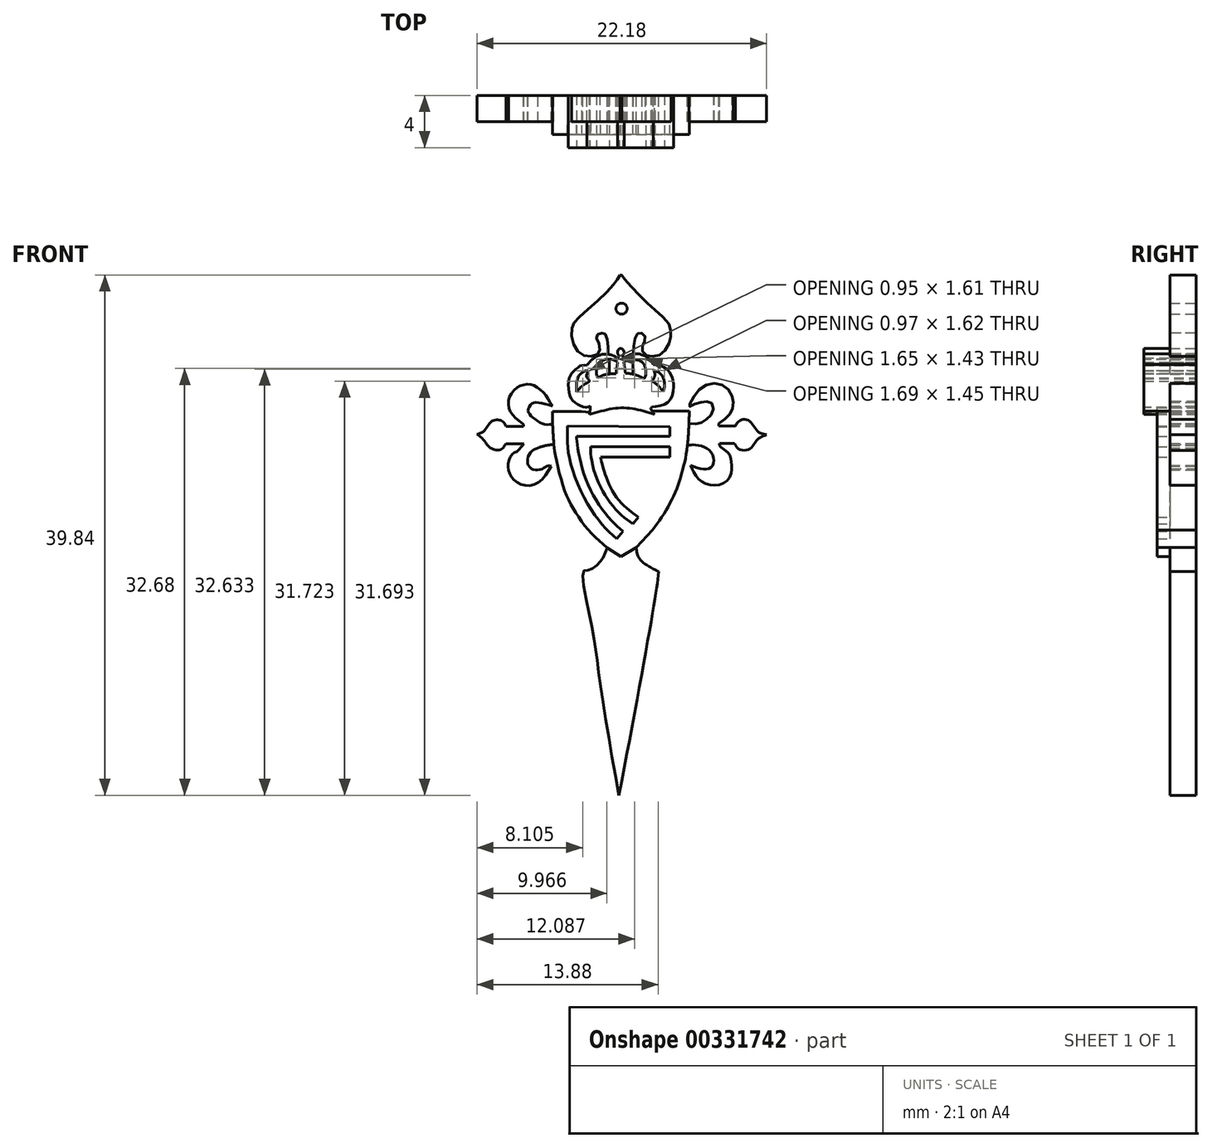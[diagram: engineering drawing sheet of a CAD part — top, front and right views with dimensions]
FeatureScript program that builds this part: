
annotation { "Feature Type Name" : "Feature", "Feature Type Description" : "" }
export const myFeature = defineFeature(function(context is Context, id is Id, definition is map)
    precondition{}
    {
        {
            var Q0;
            Q0=qCreatedBy(makeId("Front.planeOp"),FACE);
            var sketch = newSketch(context, id + "F0", { "sketchPlane" : qUnion([Q0])});
            skPoint(sketch, "E0.7.internal.snap0", {"position": v(-12.21, 0) * mm});
            skFitSpline(sketch, "E0", {"points": [v(-13.1, 18.95) * mm, v(-13.44, 18.18) * mm, v(-13.89, 17.63) * mm, v(-14.59, 17.23) * mm, v(-14.94, 17.13) * mm, v(-14.34, 13.19) * mm, v(-13.74, 9.24) * mm, v(-12.21, 0) * mm], "startDerivative": vector(-3.46, -9.08) * mm, "endDerivative": vector(6.22, -33.66) * mm});
            skFitSpline(sketch, "E1", {"points": [v(-12.21, 0) * mm, v(-9.51, 14.73) * mm, v(-9.16, 17.13) * mm], "startDerivative": vector(4.73, 24.16) * mm, "endDerivative": vector(0.84, 6.55) * mm});
            skFitSpline(sketch, "E2", {"points": [v(-9.16, 17.13) * mm, v(-9.97, 17.55) * mm, v(-10.68, 18.18) * mm, v(-10.9, 18.97) * mm], "startDerivative": vector(-2.4, 1.14) * mm, "endDerivative": vector(-0.33, 2.58) * mm});
            skFitSpline(sketch, "E3", {"points": [v(-10.9, 18.97) * mm, v(-12.07, 18.28) * mm], "startDerivative": vector(-1.18, -0.68) * mm, "endDerivative": vector(-1.18, -0.68) * mm});
            skFitSpline(sketch, "E4", {"points": [v(-13.1, 18.95) * mm, v(-12.07, 18.28) * mm], "startDerivative": vector(1.04, -0.67) * mm, "endDerivative": vector(1.04, -0.67) * mm});
            skFitSpline(sketch, "E5", {"points": [v(-13.1, 18.95) * mm, v(-14.59, 20.35) * mm, v(-15.72, 21.96) * mm, v(-16.47, 23.62) * mm, v(-17.1, 26.19) * mm, v(-17.2, 27.07) * mm, v(-17.3, 28.41) * mm, v(-17.31, 29.4) * mm], "startDerivative": vector(-9.68, 8.24) * mm, "endDerivative": vector(-0.07, 8.24) * mm});
            skFitSpline(sketch, "E6", {"points": [v(-10.9, 18.97) * mm, v(-9.64, 20.3) * mm], "startDerivative": vector(1.25, 1.34) * mm, "endDerivative": vector(1.25, 1.34) * mm});
            skFitSpline(sketch, "E7", {"points": [v(-9.64, 20.3) * mm, v(-8.68, 21.71) * mm, v(-7.88, 23.27) * mm, v(-7.35, 24.84) * mm, v(-7, 26.54) * mm, v(-6.85, 28.48) * mm, v(-6.83, 29.42) * mm], "startDerivative": vector(5.8, 8.01) * mm, "endDerivative": vector(0.09, 6.64) * mm});
            skFitSpline(sketch, "E8", {"points": [v(-17.31, 29.4) * mm, v(-15.09, 29.4) * mm], "startDerivative": vector(2.23, 0) * mm, "endDerivative": vector(2.23, 0) * mm});
            skFitSpline(sketch, "E9", {"points": [v(-6.83, 29.42) * mm, v(-9.14, 29.42) * mm], "startDerivative": vector(-2.31, 0) * mm, "endDerivative": vector(-2.31, 0) * mm});
            skFitSpline(sketch, "E10", {"points": [v(-17.3, 28.41) * mm, v(-17.94, 28.41) * mm, v(-18.45, 28.66) * mm, v(-18.98, 29.1) * mm, v(-19.15, 29.4) * mm, v(-19.1, 29.73) * mm, v(-18.84, 30) * mm, v(-18.36, 30.07) * mm, v(-17.3, 29.81) * mm], "startDerivative": vector(-5, -0.45) * mm, "endDerivative": vector(6.48, -1.86) * mm});
            skFitSpline(sketch, "E11", {"points": [v(-17.3, 29.81) * mm, v(-17.7, 30.43) * mm, v(-18.06, 30.9) * mm, v(-18.59, 31.3) * mm, v(-18.98, 31.47) * mm, v(-19.6, 31.41) * mm, v(-20.02, 31.22) * mm, v(-20.5, 30.68) * mm, v(-20.67, 30.15) * mm, v(-20.61, 29.59) * mm, v(-20.28, 29.05) * mm, v(-19.52, 28.4) * mm], "startDerivative": vector(-3.97, 6.53) * mm, "endDerivative": vector(7.28, -5.63) * mm});
            skFitSpline(sketch, "E12", {"points": [v(-19.52, 28.4) * mm, v(-19.52, 28.18) * mm], "startDerivative": vector(0, -0.22) * mm, "endDerivative": vector(0, -0.22) * mm});
            skFitSpline(sketch, "E13", {"points": [v(-19.52, 28.26) * mm, v(-20.87, 28.26) * mm], "startDerivative": vector(-1.35, 0) * mm, "endDerivative": vector(-1.35, 0) * mm});
            skFitSpline(sketch, "E14", {"points": [v(-20.87, 28.26) * mm, v(-21.15, 28.66) * mm, v(-21.51, 28.74) * mm, v(-21.93, 28.66) * mm, v(-22.27, 28.26) * mm, v(-22.6, 27.84) * mm, v(-23.09, 27.65) * mm], "startDerivative": vector(-1.46, 2.85) * mm, "endDerivative": vector(-2.96, -0.84) * mm});
            skFitSpline(sketch, "E15", {"points": [v(-23.09, 27.65) * mm, v(-22.64, 27.28) * mm, v(-22.16, 26.7) * mm, v(-21.7, 26.47) * mm, v(-21.23, 26.5) * mm, v(-20.87, 26.92) * mm], "startDerivative": vector(2.3, -1.54) * mm, "endDerivative": vector(1.63, 2.61) * mm});
            skFitSpline(sketch, "E16", {"points": [v(-20.87, 26.92) * mm, v(-19.49, 26.92) * mm], "startDerivative": vector(1.38, 0) * mm, "endDerivative": vector(1.38, 0) * mm});
            skFitSpline(sketch, "E17", {"points": [v(-19.49, 26.92) * mm, v(-20, 26.36) * mm, v(-20.33, 26.16) * mm, v(-20.67, 25.54) * mm, v(-20.67, 24.95) * mm, v(-20.36, 24.25) * mm, v(-19.49, 23.74) * mm, v(-18.36, 23.97) * mm, v(-17.4, 25.2) * mm], "startDerivative": vector(-4.32, -5.68) * mm, "endDerivative": vector(4.95, 8.5) * mm});
            skFitSpline(sketch, "E18", {"points": [v(-17.4, 25.2) * mm, v(-17.7, 25.2) * mm, v(-18.14, 24.98) * mm, v(-18.84, 24.98) * mm, v(-19.2, 25.46) * mm, v(-19.01, 26.21) * mm, v(-18.42, 26.6) * mm], "startDerivative": vector(-2.4, 0.38) * mm, "endDerivative": vector(3.59, 1.63) * mm});
            skFitSpline(sketch, "E19", {"points": [v(-17.2, 26.87) * mm, v(-17.7, 26.8) * mm, v(-18.42, 26.6) * mm], "startDerivative": vector(-1.06, -0.09) * mm, "endDerivative": vector(-1.39, -0.42) * mm});
            skFitSpline(sketch, "E20", {"points": [v(-6.85, 28.48) * mm, v(-6.05, 28.48) * mm, v(-5.5, 28.8) * mm, v(-5.01, 29.42) * mm, v(-5.16, 30.07) * mm, v(-5.72, 30.12) * mm, v(-6.45, 29.95) * mm, v(-6.83, 29.76) * mm, v(-6.48, 30.54) * mm, v(-5.46, 31.44) * mm, v(-4.23, 31.39) * mm, v(-3.55, 30.57) * mm, v(-3.47, 29.78) * mm, v(-3.75, 29.14) * mm, v(-4.57, 28.48) * mm], "startDerivative": vector(11.98, -1.22) * mm, "endDerivative": vector(-11.46, -7.82) * mm});
            skFitSpline(sketch, "E21", {"points": [v(-4.57, 28.48) * mm, v(-4.57, 28.18) * mm], "startDerivative": vector(0, -0.3) * mm, "endDerivative": vector(0, -0.3) * mm});
            skFitSpline(sketch, "E22", {"points": [v(-4.57, 28.28) * mm, v(-3.3, 28.28) * mm], "startDerivative": vector(1.26, 0) * mm, "endDerivative": vector(1.26, 0) * mm});
            skFitSpline(sketch, "E23", {"points": [v(-3.3, 28.28) * mm, v(-2.96, 28.69) * mm, v(-2.26, 28.69) * mm, v(-1.59, 27.87) * mm, v(-0.91, 27.62) * mm], "startDerivative": vector(1.23, 2.21) * mm, "endDerivative": vector(2.92, -0.45) * mm});
            skFitSpline(sketch, "E24", {"points": [v(-3.36, 26.95) * mm, v(-3.05, 26.52) * mm, v(-2.23, 26.5) * mm, v(-1.78, 27.03) * mm, v(-1.47, 27.34) * mm, v(-0.91, 27.62) * mm], "startDerivative": vector(1.14, -2.62) * mm, "endDerivative": vector(3.03, 1.34) * mm});
            skFitSpline(sketch, "E25", {"points": [v(-3.36, 26.95) * mm, v(-4.5, 26.95) * mm], "startDerivative": vector(-1.15, 0) * mm, "endDerivative": vector(-1.15, 0) * mm});
            skFitSpline(sketch, "E26", {"points": [v(-4.5, 26.95) * mm, v(-4.5, 26.78) * mm, v(-3.78, 26.13) * mm, v(-3.6, 25.57) * mm, v(-3.6, 24.67) * mm, v(-4.26, 23.88) * mm, v(-5.46, 23.83) * mm, v(-6.3, 24.44) * mm, v(-6.73, 25.26) * mm], "startDerivative": vector(-1.03, -2.6) * mm, "endDerivative": vector(-2.62, 6.35) * mm});
            skFitSpline(sketch, "E27", {"points": [v(-6.73, 25.26) * mm, v(-5.58, 24.98) * mm, v(-5.04, 25.26) * mm, v(-5.07, 26.13) * mm, v(-5.75, 26.7) * mm, v(-6.61, 26.83) * mm, v(-6.97, 26.78) * mm], "startDerivative": vector(5.97, -2.13) * mm, "endDerivative": vector(-2.8, -0.66) * mm});
            skFitSpline(sketch, "E28", {"points": [v(-14.4, 29.57) * mm, v(-14.48, 29.16) * mm], "startDerivative": vector(-0.2, -0.54) * mm, "endDerivative": vector(-0.2, -0.54) * mm});
            skFitSpline(sketch, "E29", {"points": [v(-15.09, 29.4) * mm, v(-14.42, 29.34) * mm], "startDerivative": vector(0.62, -0.06) * mm, "endDerivative": vector(0.62, -0.06) * mm});
            skFitSpline(sketch, "E30", {"points": [v(-9.48, 29.16) * mm, v(-11.9, 29.67) * mm, v(-14.48, 29.16) * mm], "startDerivative": vector(-4.85, 1.54) * mm, "endDerivative": vector(-5.21, -1.52) * mm});
            skFitSpline(sketch, "E31", {"points": [v(-14.4, 29.57) * mm, v(-14.4, 29.8) * mm], "startDerivative": vector(0, 0.24) * mm, "endDerivative": vector(0, 0.24) * mm});
            skFitSpline(sketch, "E32", {"points": [v(-14.4, 29.8) * mm, v(-14.76, 29.7) * mm, v(-15.33, 29.92) * mm, v(-15.8, 30.29) * mm, v(-16.06, 30.99) * mm, v(-16.04, 31.86) * mm, v(-15.81, 32.32) * mm, v(-15.38, 32.74) * mm, v(-15.07, 32.92) * mm, v(-14.68, 32.92) * mm], "startDerivative": vector(-3.74, -1.9) * mm, "endDerivative": vector(4.4, -0.44) * mm});
            skFitSpline(sketch, "E33", {"points": [v(-14.68, 32.92) * mm, v(-14.4, 33.24) * mm, v(-14.08, 33.5) * mm, v(-13.62, 33.73) * mm, v(-13.13, 33.78) * mm, v(-12.66, 33.67) * mm, v(-12.32, 33.49) * mm], "startDerivative": vector(1.7, 2.06) * mm, "endDerivative": vector(2.06, -1.25) * mm});
            skFitSpline(sketch, "E34", {"points": [v(-12.32, 33.49) * mm, v(-12.2, 33.64) * mm, v(-12.32, 33.87) * mm, v(-12.11, 34.22) * mm, v(-11.8, 33.91) * mm, v(-11.93, 33.65) * mm, v(-11.84, 33.49) * mm], "startDerivative": vector(1.4, 1.13) * mm, "endDerivative": vector(1.15, -1.22) * mm});
            skFitSpline(sketch, "E35", {"points": [v(-11.84, 33.49) * mm, v(-11.39, 33.73) * mm, v(-10.8, 33.81) * mm, v(-10.13, 33.59) * mm, v(-9.77, 33.3) * mm, v(-9.59, 32.99) * mm], "startDerivative": vector(2.16, 1.35) * mm, "endDerivative": vector(0.4, -1.94) * mm});
            skFitSpline(sketch, "E36", {"points": [v(-9.59, 32.99) * mm, v(-9.44, 32.99) * mm, v(-9.26, 32.99) * mm, v(-8.86, 32.83) * mm, v(-8.56, 32.63) * mm, v(-8.3, 32.32) * mm, v(-8.07, 31.75) * mm, v(-8.03, 31.23) * mm, v(-8.28, 30.3) * mm, v(-9.12, 29.82) * mm, v(-9.77, 29.66) * mm, v(-9.48, 29.16) * mm], "startDerivative": vector(2.93, -0.08) * mm, "endDerivative": vector(5.25, -6.05) * mm});
            skFitSpline(sketch, "E37", {"points": [v(-9.14, 29.42) * mm, v(-9.69, 29.42) * mm], "startDerivative": vector(-0.55, 0) * mm, "endDerivative": vector(-0.55, 0) * mm});
            skFitSpline(sketch, "E38", {"points": [v(-15.44, 30.89) * mm, v(-14.83, 31.5) * mm, v(-14.48, 31.71) * mm, v(-14.67, 32.05) * mm, v(-14.57, 32.5) * mm], "startDerivative": vector(1.77, 2.17) * mm, "endDerivative": vector(0.96, 1.93) * mm});
            skFitSpline(sketch, "E39", {"points": [v(-14.57, 32.5) * mm, v(-14.74, 32.5) * mm, v(-15.08, 32.33) * mm, v(-15.4, 31.86) * mm, v(-15.44, 30.89) * mm], "startDerivative": vector(-1.04, 0.12) * mm, "endDerivative": vector(0.15, -2.97) * mm});
            skFitSpline(sketch, "E40", {"points": [v(-13.84, 31.96) * mm, v(-13.49, 32.15) * mm, v(-12.88, 32.27) * mm, v(-12.45, 32.27) * mm], "startDerivative": vector(1.03, 0.66) * mm, "endDerivative": vector(1.26, -0.06) * mm});
            skFitSpline(sketch, "E41", {"points": [v(-12.45, 32.27) * mm, v(-12.3, 33.13) * mm], "startDerivative": vector(0.15, 0.87) * mm, "endDerivative": vector(0.15, 0.87) * mm});
            skFitSpline(sketch, "E42", {"points": [v(-12.3, 33.13) * mm, v(-12.45, 33.26) * mm, v(-12.85, 33.39) * mm, v(-13.28, 33.37) * mm, v(-13.59, 33.22) * mm, v(-13.82, 32.97) * mm, v(-13.95, 32.5) * mm, v(-13.84, 31.96) * mm], "startDerivative": vector(-1.21, 1.25) * mm, "endDerivative": vector(0.97, -3.11) * mm});
            skFitSpline(sketch, "E43", {"points": [v(-11.85, 33.18) * mm, v(-11.72, 32.3) * mm], "startDerivative": vector(0.13, -0.88) * mm, "endDerivative": vector(0.13, -0.88) * mm});
            skFitSpline(sketch, "E44", {"points": [v(-11.72, 32.3) * mm, v(-11.5, 32.3) * mm, v(-11.06, 32.23) * mm, v(-10.56, 32.05) * mm, v(-10.32, 31.9) * mm], "startDerivative": vector(1.02, 0.03) * mm, "endDerivative": vector(0.94, -0.64) * mm});
            skFitSpline(sketch, "E45", {"points": [v(-10.32, 31.9) * mm, v(-10.2, 32.06) * mm, v(-10.19, 32.7) * mm, v(-10.48, 33.2) * mm, v(-11.05, 33.36) * mm, v(-11.85, 33.18) * mm], "startDerivative": vector(1.17, 0.9) * mm, "endDerivative": vector(-3.15, -1.73) * mm});
            skFitSpline(sketch, "E46", {"points": [v(-9.55, 32.53) * mm, v(-9.47, 32.12) * mm, v(-9.7, 31.7) * mm], "startDerivative": vector(0.5, -0.82) * mm, "endDerivative": vector(-0.76, -0.84) * mm});
            skFitSpline(sketch, "E47", {"points": [v(-9.7, 31.7) * mm, v(-9.37, 31.52) * mm, v(-8.8, 30.91) * mm], "startDerivative": vector(0.79, -0.34) * mm, "endDerivative": vector(0.97, -1.19) * mm});
            skFitSpline(sketch, "E48", {"points": [v(-8.8, 30.91) * mm, v(-8.73, 31.4) * mm, v(-8.8, 31.92) * mm, v(-9.07, 32.32) * mm, v(-9.55, 32.53) * mm], "startDerivative": vector(0.47, 1.95) * mm, "endDerivative": vector(-2.08, 0.66) * mm});
            skLineSegment(sketch, "E49", {"start": v(-12.95, 33.4) * mm, "end": v(-12.95, 32.26) * mm});
            skLineSegment(sketch, "E50", {"start": v(-11.15, 33.36) * mm, "end": v(-11.15, 32.23) * mm});
            skFitSpline(sketch, "E51", {"points": [v(-11.12, 33.8) * mm, v(-11.05, 34.7) * mm, v(-10.85, 35.3) * mm, v(-10.61, 35.41) * mm, v(-10.36, 35.34) * mm, v(-10.18, 35.03) * mm, v(-10.31, 34.64) * mm, v(-10.43, 34.28) * mm, v(-10.33, 33.85) * mm, v(-9.88, 33.63) * mm, v(-9.24, 33.66) * mm, v(-8.66, 34.08) * mm, v(-8.3, 34.9) * mm, v(-8.23, 35.39) * mm, v(-8.4, 36.11) * mm, v(-9.38, 37.11) * mm, v(-10.6, 38.23) * mm, v(-11.78, 39.53) * mm, v(-12.01, 39.84) * mm], "startDerivative": vector(0.64, 14.06) * mm, "endDerivative": vector(-4.1, 5.96) * mm});
            skFitSpline(sketch, "E52", {"points": [v(-12.01, 39.84) * mm, v(-12.13, 39.84) * mm], "startDerivative": vector(-0.12, 0) * mm, "endDerivative": vector(-0.12, 0) * mm});
            skFitSpline(sketch, "E53", {"points": [v(-13.06, 33.77) * mm, v(-13.05, 34.63) * mm, v(-13.22, 35.26) * mm, v(-13.4, 35.37) * mm, v(-13.6, 35.39) * mm, v(-13.84, 35.27) * mm, v(-13.94, 35.08) * mm, v(-13.76, 34.66) * mm, v(-13.67, 34.1) * mm, v(-13.89, 33.75) * mm, v(-14.6, 33.6) * mm, v(-15.31, 33.94) * mm, v(-15.78, 34.84) * mm, v(-15.8, 35.8) * mm, v(-15.59, 36.25) * mm, v(-14.52, 37.26) * mm, v(-12.8, 38.87) * mm, v(-12.36, 39.47) * mm, v(-12.13, 39.84) * mm], "startDerivative": vector(0.92, 13.2) * mm, "endDerivative": vector(5.07, 7.88) * mm});
            skFitSpline(sketch, "E54", {"points": [v(-8.3, 28.23) * mm, v(-16.16, 28.26) * mm], "startDerivative": vector(-7.86, 0.04) * mm, "endDerivative": vector(-7.86, 0.04) * mm});
            skFitSpline(sketch, "E55", {"points": [v(-16.16, 28.26) * mm, v(-16.16, 27.55) * mm, v(-15.91, 25.41) * mm, v(-14.11, 21.53) * mm, v(-12.39, 19.64) * mm], "startDerivative": vector(-0.02, -4.5) * mm, "endDerivative": vector(6.45, -5.99) * mm});
            skFitSpline(sketch, "E56", {"points": [v(-12.39, 19.64) * mm, v(-11.9, 20.22) * mm], "startDerivative": vector(0.49, 0.58) * mm, "endDerivative": vector(0.49, 0.58) * mm});
            skFitSpline(sketch, "E57", {"points": [v(-11.9, 20.22) * mm, v(-12.82, 21.08) * mm, v(-14.06, 22.77) * mm, v(-15.03, 25.06) * mm, v(-15.4, 26.91) * mm, v(-15.46, 27.48) * mm], "startDerivative": vector(-5.02, 4.33) * mm, "endDerivative": vector(-0.32, 4.02) * mm});
            skFitSpline(sketch, "E58", {"points": [v(-15.46, 27.48) * mm, v(-8.3, 27.48) * mm], "startDerivative": vector(7.17, 0) * mm, "endDerivative": vector(7.17, 0) * mm});
            skFitSpline(sketch, "E59", {"points": [v(-8.3, 28.23) * mm, v(-8.3, 27.48) * mm], "startDerivative": vector(0, -0.75) * mm, "endDerivative": vector(0, -0.75) * mm});
            skFitSpline(sketch, "E60", {"points": [v(-8.3, 26.7) * mm, v(-8.3, 25.9) * mm], "startDerivative": vector(0, -0.8) * mm, "endDerivative": vector(0, -0.8) * mm});
            skFitSpline(sketch, "E61", {"points": [v(-8.3, 26.7) * mm, v(-14.37, 26.7) * mm], "startDerivative": vector(-6.25, 0) * mm, "endDerivative": vector(-6.25, 0) * mm});
            skFitSpline(sketch, "E62", {"points": [v(-8.3, 25.9) * mm, v(-13.61, 25.9) * mm], "startDerivative": vector(-5.31, 0) * mm, "endDerivative": vector(-5.31, 0) * mm});
            skFitSpline(sketch, "E63", {"points": [v(-10.71, 21.3) * mm, v(-11.5, 21.9) * mm, v(-12.54, 23.03) * mm, v(-13.2, 24.38) * mm, v(-13.48, 25.28) * mm, v(-13.61, 25.9) * mm], "startDerivative": vector(-4, 2.82) * mm, "endDerivative": vector(-0.77, 3.97) * mm});
            skFitSpline(sketch, "E64", {"points": [v(-14.37, 26.7) * mm, v(-14.37, 26.19) * mm, v(-14.06, 24.67) * mm, v(-13.18, 22.85) * mm, v(-12.13, 21.56) * mm, v(-11.13, 20.78) * mm], "startDerivative": vector(-0.4, -3.77) * mm, "endDerivative": vector(5.21, -3.66) * mm});
            skFitSpline(sketch, "E65", {"points": [v(-10.71, 21.3) * mm, v(-11.13, 20.78) * mm], "startDerivative": vector(-0.42, -0.52) * mm, "endDerivative": vector(-0.42, -0.52) * mm});
            skCircle(sketch, "E66", {"center": v(-12.01, 37.26) * mm, "radius": 0.43 * mm});
            skSolve(sketch);
        }
        {
            var Q0;
            Q0=makeQuery(id+"F0.imprint","IMPRINT",FACE,{"disambiguationData":[TD([[makeQuery(id+"F0.imprint","IMPRINT",EDGE,{"derivedFrom":sQuery(id+"F0.wireOp",EDGE,"E3")}),-1.0]])]});
            extrude(context, id + "F1", {"entities" : qUnion([Q0]), "depth" : 3 * mm});
        }
        {
            var Q0;
            {var subQ1=sQuery(id+"F0.wireOp",EDGE,"E10");Q0=makeQuery(id+"F0.imprint","IMPRINT",FACE,{"disambiguationData":[TD([[makeQuery(id+"F0.imprint","IMPRINT",EDGE,{"derivedFrom":subQ1}),1.0]])]});}
            var Q1;
            {var subQ1=sQuery(id+"F0.wireOp",EDGE,"E20");Q1=makeQuery(id+"F0.imprint","IMPRINT",FACE,{"disambiguationData":[TD([[makeQuery(id+"F0.imprint","IMPRINT",EDGE,{"derivedFrom":subQ1}),-1.0]])]});}
            var Q2;
            {var subQ2=sQuery(id+"F0.wireOp",EDGE,"E34");Q2=makeQuery(id+"F0.imprint","IMPRINT",FACE,{"disambiguationData":[TD([[makeQuery(id+"F0.imprint","IMPRINT",EDGE,{"derivedFrom":subQ2}),1.0]])]});}
            var Q3;
            Q3=makeQuery(id+"F0.imprint","IMPRINT",FACE,{"disambiguationData":[TD([[makeQuery(id+"F0.imprint","IMPRINT",EDGE,{"derivedFrom":sQuery(id+"F0.wireOp",EDGE,"E3")}),-1.0]])]});
            var Q4;
            Q4=makeQuery(id+"F0.imprint","IMPRINT",FACE,{"disambiguationData":[TD([[makeQuery(id+"F0.imprint","IMPRINT",EDGE,{"derivedFrom":sQuery(id+"F0.wireOp",EDGE,"E60")}),-1.0]])]});
            var Q5;
            Q5=makeQuery(id+"F0.imprint","IMPRINT",FACE,{"disambiguationData":[TD([[makeQuery(id+"F0.imprint","IMPRINT",EDGE,{"derivedFrom":sQuery(id+"F0.wireOp",EDGE,"E54")}),1.0]])]});
            var Q6;
            Q6=makeQuery(id+"F0.imprint","IMPRINT",FACE,{"disambiguationData":[TD([[makeQuery(id+"F0.imprint","IMPRINT",EDGE,{"derivedFrom":sQuery(id+"F0.wireOp",EDGE,"E0")}),1.0]])]});
            var Q7;
            {var subQ0=sQuery(id+"F0.wireOp",EDGE,"E41");Q7=makeQuery(id+"F0.imprint","IMPRINT",FACE,{"disambiguationData":[TD([[makeQuery(id+"F0.imprint","IMPRINT",EDGE,{"derivedFrom":subQ0}),1.0]])]});}
            var Q8;
            {var subQ0=sQuery(id+"F0.wireOp",EDGE,"E43");Q8=makeQuery(id+"F0.imprint","IMPRINT",FACE,{"disambiguationData":[TD([[makeQuery(id+"F0.imprint","IMPRINT",EDGE,{"derivedFrom":subQ0}),1.0]])]});}
            extrude(context, id + "F2", {"entities" : qUnion([Q0, Q1, Q2, Q3, Q4, Q5, Q6, Q7, Q8]), "operationType" : NewBodyOperationType.ADD, "depth" : 2 * mm});
        }
        {
            var Q0;
            {var subQ12=sQuery(id+"F0.wireOp",EDGE,"E30");Q0=makeQuery(id+"F0.imprint","IMPRINT",FACE,{"disambiguationData":[TD([[makeQuery(id+"F0.imprint","IMPRINT",EDGE,{"derivedFrom":subQ12}),-1.0]])]});}
            extrude(context, id + "F3", {"entities" : qUnion([Q0]), "depth" : 4 * mm});
        }
    });
